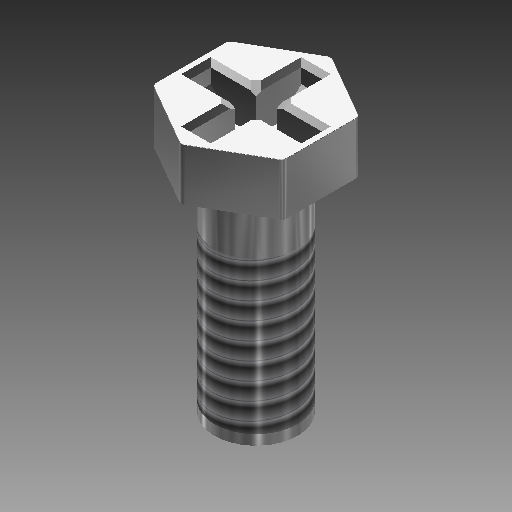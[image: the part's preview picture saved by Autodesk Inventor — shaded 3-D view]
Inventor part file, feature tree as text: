
AUTODESK INVENTOR PART (.ipt)
format: ipt  version: 2019 (Build 230136000, 136)  size: 241,664 bytes
history: native  units: in
note: dims shown in document units (in); Inventor stores cm internally (conversion verified against a paired STEP export)
features: chamfer x4, extrude x3, sketch x3, fillet x2, thread x1
ambient origin geometry x8: Origin, YZ Plane, XZ Plane, XY Plane, X Axis, Y Axis, Z Axis, Center Point
bodies: Solid1 (feature_tree)
feature tree (13):
  extrude  "Extrusion1"  Depth=0.391in TaperAngle=0.0deg
  thread  "Thread1"  [1 undecoded]
  extrude  "Extrusion2"  Depth=0.094in TaperAngle=0.0deg
  fillet  "Fillet1"  Radius=0.01in
  fillet  "Fillet2"  Radius=0.001in
  extrude  "Extrusion3"  Depth=0.037in
  chamfer  "Chamfer1"  Distance=0.2in
  chamfer  "Chamfer2"  Distance=0.2in
  chamfer  "Chamfer3"  Distance=0.0178in
  chamfer  "Chamfer4"  Distance=0.0168in
  sketch  "Sketch1"  dims[d0=0.15in d1=0.391in d2=0.0in d3=0.273in d4=0.1in]
  sketch  "Sketch2"  dims[d7=0.272in d8=0.094in d9=0.0in d10=0.01in d11=0.001in]
  sketch  "Sketch3"  dims[d12=0.037in d13=0.037in d14=0.2in d15=0.2in d16=0.0178in d17=0.0168in d18=0.074in d19=0.0in d20=0.008in d21=0.125in d22=45.0deg d23=0.008in d24=0.125in d25=45.0deg d26=0.04in d27=0.125in d28=45.0deg d29=0.04in d30=0.125in d31=45.0deg]
note: 1 required parameter value undecoded (feature->parameter linkage not recoverable at this tier; creation-order binding heuristic only, values carry confidence <= 0.55)
